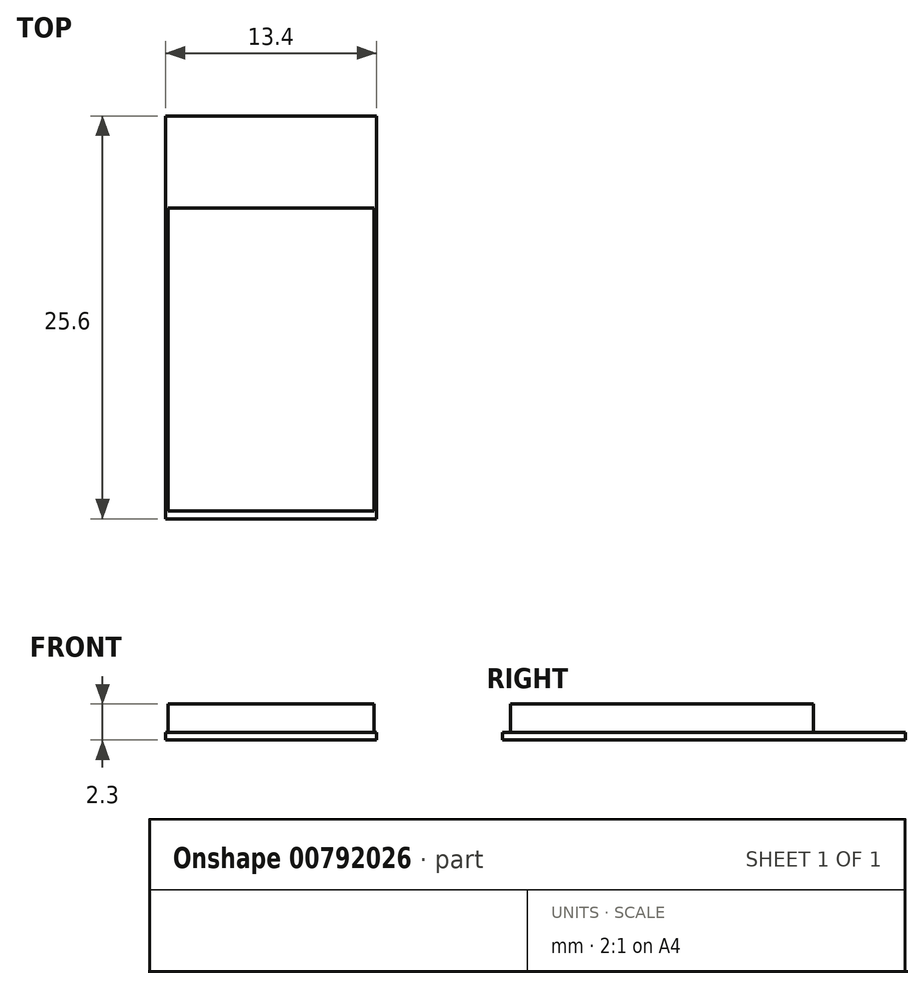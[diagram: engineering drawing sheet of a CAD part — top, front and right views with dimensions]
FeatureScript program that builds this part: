
annotation { "Feature Type Name" : "Feature", "Feature Type Description" : "" }
export const myFeature = defineFeature(function(context is Context, id is Id, definition is map)
    precondition{}
    {
        {
            var Q0;
            Q0=qCreatedBy(makeId("Top.planeOp"),FACE);
            var sketch = newSketch(context, id + "F0", { "sketchPlane" : qUnion([Q0])});
            skLineSegment(sketch, "E0.bottom", {"start": v(0, 0) * mm, "end": v(13.4, 0) * mm});
            skLineSegment(sketch, "E0.top", {"start": v(0, 25.6) * mm, "end": v(13.4, 25.6) * mm});
            skLineSegment(sketch, "E0.left", {"start": v(0, 0) * mm, "end": v(0, 25.6) * mm});
            skLineSegment(sketch, "E0.right", {"start": v(13.4, 0) * mm, "end": v(13.4, 25.6) * mm});
            skSolve(sketch);
        }
        {
            var Q0;
            Q0=makeQuery(id+"F0.imprint","IMPRINT",FACE,{"disambiguationData":[TD([[makeQuery(id+"F0.imprint","IMPRINT",EDGE,{"derivedFrom":sQuery(id+"F0.wireOp",EDGE,"E0.bottom")}),1.0]])]});
            extrude(context, id + "F1", {"entities" : qUnion([Q0]), "depth" : .5 * mm, "offsetDistance" : 25 * mm});
        }
        {
            var Q0;
            Q0=makeQuery(id+"F1.opExtrude","CAP_FACE",FACE,{"disambiguationData":[OSD([sQuery(id+"F0.wireOp",EDGE,"E0.bottom"),sQuery(id+"F0.wireOp",EDGE,"E0.top"),sQuery(id+"F0.wireOp",EDGE,"E0.left"),sQuery(id+"F0.wireOp",EDGE,"E0.right")])],"isStart":false});
            var sketch = newSketch(context, id + "F2", { "sketchPlane" : qUnion([Q0])});
            skLineSegment(sketch, "E1.bottom", {"start": v(0.15, 0.5) * mm, "end": v(13.25, 0.5) * mm});
            skLineSegment(sketch, "E1.top", {"start": v(0.15, 19.75) * mm, "end": v(13.25, 19.75) * mm});
            skLineSegment(sketch, "E1.left", {"start": v(0.15, 0.5) * mm, "end": v(0.15, 19.75) * mm});
            skLineSegment(sketch, "E1.right", {"start": v(13.25, 0.5) * mm, "end": v(13.25, 19.75) * mm});
            skSolve(sketch);
        }
        {
            var Q0;
            Q0=qSketchRegion(id+"F2",true);
            extrude(context, id + "F3", {"entities" : qUnion([Q0]), "operationType" : NewBodyOperationType.ADD, "depth" : (2.3 - .5) * mm, "offsetDistance" : 25 * mm});
        }
    });
